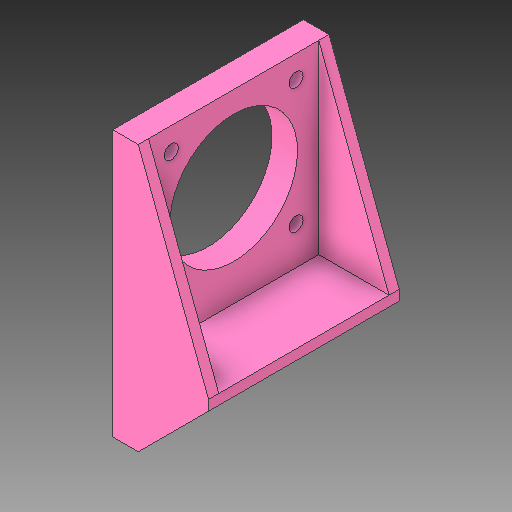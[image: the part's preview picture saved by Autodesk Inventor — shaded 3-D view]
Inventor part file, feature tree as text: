
AUTODESK INVENTOR PART (.ipt)
format: ipt  version: 2019 (Build 230136000, 136)  size: 194,048 bytes
history: native  units: in
note: dims shown in document units (in); Inventor stores cm internally (conversion verified against a paired STEP export)
features: extrude x3, sketch x3, projected_geometry x2
ambient origin geometry x8: Origin, YZ Plane, XZ Plane, XY Plane, X Axis, Y Axis, Z Axis, Center Point
bodies: Body1 (feature_tree)
feature tree (8):
  extrude  "Extrusion2"  Depth=0.1378in
  extrude  "Extrusion3"  Depth=1.6654in
  extrude  "Extrusion5"  Depth=0.1in
  sketch  "Sketch2"  dims[d19=1.2205in d20=0.1378in]
  sketch  "Sketch3"  dims[d21=1.6654in d24=0.2165in]
  sketch  "Sketch5"  dims[d25=0.25in d26=0.0in d27=0.1in d28=0.1in d29=0.1in d30=0.7874in d31=0.6874in d32=0.0in d35=1.25in d36=0.9327in d38=0.7874in d39=1.6654in d40=0.15in d41=0.3937in d42=0.1in d43=1.6654in d44=0.6874in d45=0.0in]
  projected_geometry  "Projected Loop3"
  projected_geometry  "Projected Loop4"
